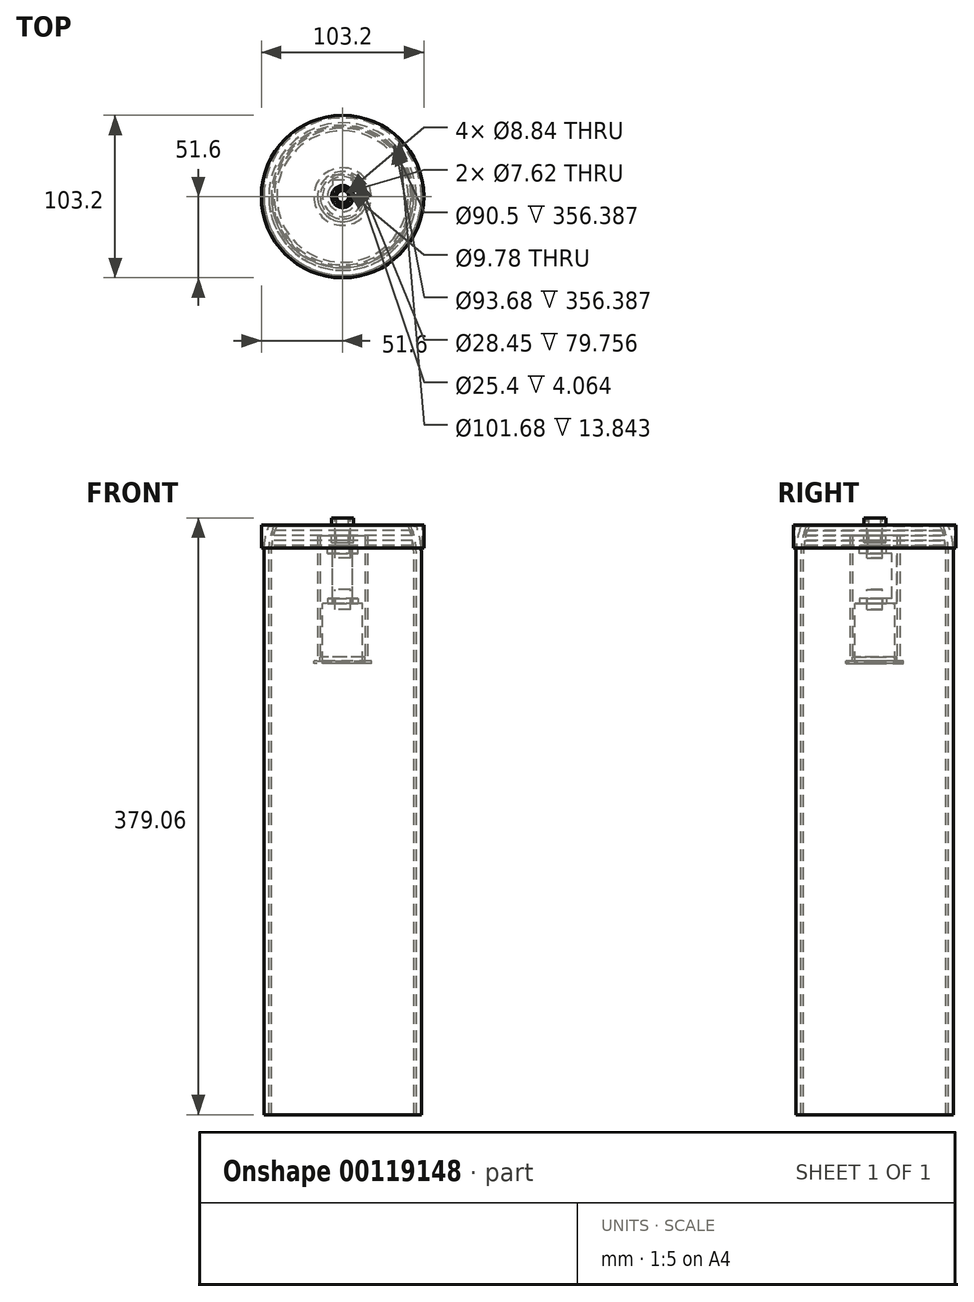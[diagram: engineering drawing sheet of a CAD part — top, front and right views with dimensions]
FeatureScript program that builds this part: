
annotation { "Feature Type Name" : "Feature", "Feature Type Description" : "" }
export const myFeature = defineFeature(function(context is Context, id is Id, definition is map)
    precondition{}
    {
        {
            var Q0;
            Q0=qCreatedBy(makeId("Front.planeOp"),FACE);
            var sketch = newSketch(context, id + "F0", { "sketchPlane" : qUnion([Q0])});
            skLineSegment(sketch, "E0", {"start": v(-50.01, -19.05) * mm, "end": v(-50.01, -375.44) * mm});
            skArc(sketch, "E1", {"start": v(-50.01, -19.05) * mm, "mid": v(-35.36, 16.31) * mm, "end": v(0, 30.96) * mm});
            skLineSegment(sketch, "E2", {"start": v(-50.01, -375.44) * mm, "end": v(0, -375.44) * mm});
            skLineSegment(sketch, "E3", {"start": v(0, 30.96) * mm, "end": v(0, -375.44) * mm});
            skSolve(sketch);
        }
        {
            var Q0;
            Q0=makeQuery(id+"F0.imprint","IMPRINT",FACE,{"disambiguationData":[TD([[makeQuery(id+"F0.imprint","IMPRINT",EDGE,{"derivedFrom":sQuery(id+"F0.wireOp",EDGE,"E0")}),1.0]])]});
            var Q1;
            Q1=sQuery(id+"F0.wireOp",EDGE,"E3");
            revolve(context, id + "F1", {"entities" : qUnion([Q0]), "axis" : qUnion([Q1]), "revolveType" : RevolveType.FULL});
        }
        {
            var Q0;
            Q0=qSketchRegion(id+"F0",true);
            var Q1;
            Q1=sQuery(id+"F0.wireOp",EDGE,"E3");
            revolve(context, id + "F2", {"entities" : qUnion([Q0]), "axis" : qUnion([Q1]), "revolveType" : RevolveType.FULL});
        }
        {
            var Q0;
            Q0=makeQuery(id+"F1.opRevolve","SWEPT_FACE",FACE,{"disambiguationData":[OSD([sQuery(id+"F0.wireOp",EDGE,"E2")])]});
            shell(context, id + "F3", {"entities" : qUnion([Q0]), "thickness" : 3.17 * mm});
        }
        {
            var Q0;
            Q0=makeQuery(id+"F2.opRevolve","SWEPT_FACE",FACE,{"disambiguationData":[OSD([sQuery(id+"F0.wireOp",EDGE,"E2")])]});
            shell(context, id + "F4", {"entities" : qUnion([Q0]), "thickness" : 4.76 * mm});
        }
        {
            var Q0;
            Q0=qCreatedBy(makeId("Front.planeOp"),FACE);
            var sketch = newSketch(context, id + "F5", { "sketchPlane" : qUnion([Q0])});
            skLineSegment(sketch, "E4", {"start": v(-97, -1.59) * mm, "end": v(106.2, -1.59) * mm});
            skArc(sketch, "E5", {"start": v(-50.01, -19.05) * mm, "mid": v(0, 30.96) * mm, "end": v(50.01, -19.05) * mm, "construction": true});
            skArc(sketch, "E6", {"start": v(-50.01, -19.05) * mm, "mid": v(0, 30.96) * mm, "end": v(50.01, -19.05) * mm});
            skSolve(sketch);
        }
        {
            var Q0;
            Q0=qSketchRegion(id+"F5",true);
            extrude(context, id + "F6", {"entities" : qUnion([Q0]), "operationType" : NewBodyOperationType.REMOVE, "endBound" : BoundingType.THROUGH_ALL, "oppositeDirection" : true, "depth" : 25.4 * mm, "hasSecondDirection" : true, "secondDirectionBound" : BoundingType.THROUGH_ALL, "secondDirectionOppositeDirection" : false, "secondDirectionDepth" : 25.4 * mm});
        }
        {
            var Q0;
            Q0=qCreatedBy(makeId("Front.planeOp"),FACE);
            var sketch = newSketch(context, id + "F7", { "sketchPlane" : qUnion([Q0])});
            skArc(sketch, "E7", {"start": v(43.46, -1.59) * mm, "mid": v(45.99, -10.16) * mm, "end": v(46.84, -19.05) * mm, "construction": true});
            skArc(sketch, "E8", {"start": v(-46.84, -19.05) * mm, "mid": v(-45.99, -10.16) * mm, "end": v(-43.46, -1.59) * mm, "construction": true});
            skLineSegment(sketch, "E9", {"start": v(-46.84, -19.05) * mm, "end": v(-46.84, -375.44) * mm, "construction": true});
            skLineSegment(sketch, "E10", {"start": v(46.84, -375.44) * mm, "end": v(46.84, -19.05) * mm, "construction": true});
            skLineSegment(sketch, "E11", {"start": v(43.46, -1.59) * mm, "end": v(46.86, -1.59) * mm, "construction": true});
            skLineSegment(sketch, "E12", {"start": v(-46.86, -1.59) * mm, "end": v(-43.46, -1.59) * mm, "construction": true});
            skArc(sketch, "E13", {"start": v(46.86, -1.59) * mm, "mid": v(49.22, -10.18) * mm, "end": v(50.01, -19.05) * mm, "construction": true});
            skArc(sketch, "E14", {"start": v(-50.01, -19.05) * mm, "mid": v(-49.22, -10.18) * mm, "end": v(-46.86, -1.59) * mm, "construction": true});
            skLineSegment(sketch, "E15", {"start": v(-50.01, -19.05) * mm, "end": v(-50.01, -375.44) * mm, "construction": true});
            skLineSegment(sketch, "E16", {"start": v(50.01, -375.44) * mm, "end": v(50.01, -19.05) * mm, "construction": true});
            skLineSegment(sketch, "E17", {"start": v(46.84, -375.44) * mm, "end": v(50.01, -375.44) * mm, "construction": true});
            skLineSegment(sketch, "E18", {"start": v(-50.01, -375.44) * mm, "end": v(-46.84, -375.44) * mm, "construction": true});
            skLineSegment(sketch, "E19", {"start": v(-51.6, -15.43) * mm, "end": v(-51.6, -0.83) * mm});
            skLineSegment(sketch, "E20", {"start": v(-51.6, -0.83) * mm, "end": v(-4.42, -0.83) * mm});
            skLineSegment(sketch, "E21", {"start": v(-4.42, -0.83) * mm, "end": v(-4.42, -1.59) * mm});
            skLineSegment(sketch, "E22", {"start": v(-44.45, -7.46) * mm, "end": v(-4.42, -7.46) * mm});
            skLineSegment(sketch, "E23", {"start": v(-4.42, -7.46) * mm, "end": v(-4.42, -4.29) * mm});
            skLineSegment(sketch, "E24", {"start": v(-51.6, -15.43) * mm, "end": v(-50.84, -15.43) * mm});
            skLineSegment(sketch, "E25", {"start": v(-44.45, -4.29) * mm, "end": v(-4.42, -4.29) * mm});
            skLineSegment(sketch, "E26", {"start": v(-50.84, -1.59) * mm, "end": v(-50.84, -15.43) * mm});
            skLineSegment(sketch, "E27", {"start": v(0, 0) * mm, "end": v(0, -375.44) * mm, "construction": true});
            skLineSegment(sketch, "E28", {"start": v(-50.84, -1.59) * mm, "end": v(-4.42, -1.59) * mm});
            skLineSegment(sketch, "E29", {"start": v(-44.45, -4.29) * mm, "end": v(-44.45, -7.46) * mm});
            skLineSegment(sketch, "E30", {"start": v(-43.73, -2.29) * mm, "end": v(43.73, -2.29) * mm, "construction": true});
            skSolve(sketch);
        }
        {
            var Q0;
            {var subQ1=sQuery(id+"F7.wireOp",EDGE,"E19");Q0=makeQuery(id+"F7.imprint","IMPRINT",FACE,{"disambiguationData":[TD([[makeQuery(id+"F7.imprint","IMPRINT",EDGE,{"derivedFrom":subQ1}),-1.0]])]});}
            var Q1;
            Q1=sQuery(id+"F7.wireOp",EDGE,"E27");
            revolve(context, id + "F8", {"entities" : qUnion([Q0]), "axis" : qUnion([Q1]), "revolveType" : RevolveType.FULL});
        }
        {
            var Q0;
            Q0=makeQuery(id+"F7.imprint","IMPRINT",FACE,{"disambiguationData":[TD([[makeQuery(id+"F7.imprint","IMPRINT",EDGE,{"derivedFrom":sQuery(id+"F7.wireOp",EDGE,"E22")}),1.0]])]});
            var Q1;
            Q1=sQuery(id+"F7.wireOp",EDGE,"E27");
            revolve(context, id + "F9", {"entities" : qUnion([Q0]), "axis" : qUnion([Q1]), "revolveType" : RevolveType.FULL});
        }
        {
            var Q0;
            Q0=makeQuery(id+"F8.opRevolve","SWEPT_FACE",FACE,{"disambiguationData":[OSD([sQuery(id+"F7.wireOp",EDGE,"E20")])]});
            cPlane(context, id + "F10", {"entities" : qUnion([Q0]), "cplaneType" : CPlaneType.OFFSET, "offset" : 4.44 * mm, "width" : 152.4 * mm, "height" : 152.4 * mm});
        }
        {
            var Q0;
            Q0=qCreatedBy(id+"F10.planeOp",FACE);
            var sketch = newSketch(context, id + "F11", { "sketchPlane" : qUnion([Q0])});
            skCircle(sketch, "E31", {"center": v(0, 0) * mm, "radius": 6.99 * mm});
            skCircle(sketch, "E32", {"center": v(0, 0) * mm, "radius": 3.81 * mm});
            skSolve(sketch);
        }
        {
            var Q0;
            Q0=makeQuery(id+"F11.imprint","IMPRINT",FACE,{"disambiguationData":[TD([[makeQuery(id+"F11.imprint","IMPRINT",EDGE,{"derivedFrom":sQuery(id+"F11.wireOp",EDGE,"E31")}),1.0]])]});
            extrude(context, id + "F12", {"entities" : qUnion([Q0]), "oppositeDirection" : true, "depth" : 4.44 * mm});
        }
        {
            var Q0;
            Q0=makeQuery(id+"F12.opExtrude","CAP_FACE",FACE,{"disambiguationData":[OSD([sQuery(id+"F11.wireOp",EDGE,"E31"),sQuery(id+"F11.wireOp",EDGE,"E32")])],"isStart":true});
            var sketch = newSketch(context, id + "F13", { "sketchPlane" : qUnion([Q0])});
            skCircle(sketch, "E33", {"center": v(0, 0) * mm, "radius": 4.93 * mm});
            skSolve(sketch);
        }
        {
            var Q0;
            Q0 = qSketchRegion(id + "F13", true);
            extrude(context, id + "F14", {"entities" : qUnion([Q0]), "oppositeDirection" : true, "depth" : 25.4 * mm});
        }
        {
            var Q0;
            Q0=makeQuery(id+"F9.opRevolve","SWEPT_FACE",FACE,{"disambiguationData":[OSD([sQuery(id+"F7.wireOp",EDGE,"E22")])]});
            var sketch = newSketch(context, id + "F15", { "sketchPlane" : qUnion([Q0])});
            skCircle(sketch, "E34", {"center": v(0, 0) * mm, "radius": 3.81 * mm});
            skCircle(sketch, "E35.0", {"center": v(0, 0) * mm, "radius": 6.99 * mm});
            skSolve(sketch);
        }
        {
            var Q0;
            Q0 = qSketchRegion(id + "F15", true);
            extrude(context, id + "F16", {"entities" : qUnion([Q0]), "depth" : 4.44 * mm});
        }
        {
            var Q0;
            Q0=makeQuery(id+"F16.opExtrude","CAP_FACE",FACE,{"disambiguationData":[OSD([sQuery(id+"F15.wireOp",EDGE,"E34"),sQuery(id+"F15.wireOp",EDGE,"E35.0")])],"isStart":false});
            cPlane(context, id + "F17", {"entities" : qUnion([Q0]), "cplaneType" : CPlaneType.OFFSET, "offset" : 3.8 * mm, "width" : 152.4 * mm, "height" : 152.4 * mm});
        }
        {
            var Q0;
            Q0=qCreatedBy(id+"F17.planeOp",FACE);
            var sketch = newSketch(context, id + "F18", { "sketchPlane" : qUnion([Q0])});
            skArc(sketch, "E36", {"start": v(6.35, -7.27) * mm, "mid": v(0, 9.65) * mm, "end": v(-6.35, -7.27) * mm});
            skCircle(sketch, "E37", {"center": v(0, 0) * mm, "radius": 4.42 * mm});
            skLineSegment(sketch, "E38.bottom", {"start": v(-6.35, -13.97) * mm, "end": v(6.35, -13.97) * mm});
            skLineSegment(sketch, "E38.left", {"start": v(-6.35, -13.97) * mm, "end": v(-6.35, -7.27) * mm});
            skLineSegment(sketch, "E38.right", {"start": v(6.35, -13.97) * mm, "end": v(6.35, -7.27) * mm});
            skSolve(sketch);
        }
        {
            var Q0;
            Q0=qSketchRegion(id+"F18",true);
            extrude(context, id + "F19", {"entities" : qUnion([Q0]), "depth" : 3.17 * mm});
        }
        {
            var Q0;
            Q0=makeQuery(id+"F19.opExtrude","CAP_FACE",FACE,{"disambiguationData":[OSD([sQuery(id+"F18.wireOp",EDGE,"E36"),sQuery(id+"F18.wireOp",EDGE,"E37"),sQuery(id+"F18.wireOp",EDGE,"E38.bottom"),sQuery(id+"F18.wireOp",EDGE,"E38.left"),sQuery(id+"F18.wireOp",EDGE,"E38.right")])],"isStart":false});
            var sketch = newSketch(context, id + "F20", { "sketchPlane" : qUnion([Q0])});
            skLineSegment(sketch, "E39.bottom", {"start": v(-6.35, -13.97) * mm, "end": v(6.35, -13.97) * mm});
            skLineSegment(sketch, "E39.top", {"start": v(-6.35, -10.8) * mm, "end": v(6.35, -10.8) * mm});
            skLineSegment(sketch, "E39.left", {"start": v(-6.35, -13.97) * mm, "end": v(-6.35, -10.8) * mm});
            skLineSegment(sketch, "E39.right", {"start": v(6.35, -13.97) * mm, "end": v(6.35, -10.8) * mm});
            skSolve(sketch);
        }
        {
            var Q0;
            Q0=qSketchRegion(id+"F20",true);
            extrude(context, id + "F21", {"entities" : qUnion([Q0]), "operationType" : NewBodyOperationType.ADD, "depth" : 31.75 * mm - 1 / 203.2 * mm});
        }
        {
            var Q0;
            Q0=makeQuery(id+"F21.opExtrude","CAP_FACE",FACE,{"disambiguationData":[OSD([sQuery(id+"F20.wireOp",EDGE,"E39.bottom"),sQuery(id+"F20.wireOp",EDGE,"E39.top"),sQuery(id+"F20.wireOp",EDGE,"E39.left"),sQuery(id+"F20.wireOp",EDGE,"E39.right")])],"isStart":false});
            var sketch = newSketch(context, id + "F22", { "sketchPlane" : qUnion([Q0])});
            skLineSegment(sketch, "E40.0.0", {"start": v(-6.35, -7.27) * mm, "end": v(-6.35, -10.8) * mm});
            skLineSegment(sketch, "E40.0.1", {"start": v(-6.35, -10.8) * mm, "end": v(6.35, -10.8) * mm});
            skLineSegment(sketch, "E40.0.2", {"start": v(6.35, -10.8) * mm, "end": v(6.35, -7.27) * mm});
            skArc(sketch, "E40.0.3", {"start": v(6.35, -7.27) * mm, "mid": v(0, 9.65) * mm, "end": v(-6.35, -7.27) * mm});
            skLineSegment(sketch, "E41.0", {"start": v(-6.35, -13.97) * mm, "end": v(6.35, -13.97) * mm});
            skLineSegment(sketch, "E41.2", {"start": v(-6.35, -13.97) * mm, "end": v(-6.35, -10.8) * mm});
            skLineSegment(sketch, "E41.3", {"start": v(6.35, -13.97) * mm, "end": v(6.35, -10.8) * mm});
            skCircle(sketch, "E42.0", {"center": v(0, 0) * mm, "radius": 4.89 * mm});
            skSolve(sketch);
        }
        {
            var Q0;
            Q0=qSketchRegion(id+"F22",true);
            extrude(context, id + "F23", {"entities" : qUnion([Q0]), "operationType" : NewBodyOperationType.ADD, "oppositeDirection" : true, "depth" : 3.17 * mm});
        }
        {
            var Q0;
            Q0=qCreatedBy(makeId("Front.planeOp"),FACE);
            var sketch = newSketch(context, id + "F24", { "sketchPlane" : qUnion([Q0])});
            skLineSegment(sketch, "E43.bottom", {"start": v(-4.93, -41.75) * mm, "end": v(4.93, -41.75) * mm});
            skLineSegment(sketch, "E43.top", {"start": v(-4.93, -54.45) * mm, "end": v(4.93, -54.45) * mm});
            skLineSegment(sketch, "E43.left", {"start": v(-4.93, -41.75) * mm, "end": v(-4.93, -54.45) * mm});
            skLineSegment(sketch, "E43.right", {"start": v(4.93, -41.75) * mm, "end": v(4.93, -54.45) * mm});
            skLineSegment(sketch, "E44", {"start": v(-4.93, 3.62) * mm, "end": v(-4.93, -21.78) * mm});
            skLineSegment(sketch, "E45", {"start": v(4.93, -21.78) * mm, "end": v(4.93, 3.62) * mm});
            skLineSegment(sketch, "E46.bottom", {"start": v(-12.7, -50.64) * mm, "end": v(12.7, -50.64) * mm});
            skLineSegment(sketch, "E46.top", {"start": v(-12.7, -88.74) * mm, "end": v(12.7, -88.74) * mm});
            skLineSegment(sketch, "E46.left", {"start": v(-12.7, -50.64) * mm, "end": v(-12.7, -88.74) * mm});
            skLineSegment(sketch, "E46.right", {"start": v(12.7, -50.64) * mm, "end": v(12.7, -88.74) * mm});
            skLineSegment(sketch, "E47", {"start": v(-12.7, -84.68) * mm, "end": v(-14.22, -84.68) * mm});
            skLineSegment(sketch, "E48", {"start": v(-14.22, -84.68) * mm, "end": v(-14.22, -87.22) * mm});
            skLineSegment(sketch, "E49", {"start": v(-14.22, -87.22) * mm, "end": v(-18.29, -87.22) * mm});
            skLineSegment(sketch, "E50", {"start": v(-18.29, -87.22) * mm, "end": v(-18.29, -88.74) * mm});
            skLineSegment(sketch, "E51", {"start": v(-18.29, -88.74) * mm, "end": v(-12.7, -88.74) * mm});
            skLineSegment(sketch, "E52", {"start": v(0, -41.75) * mm, "end": v(0, -88.74) * mm});
            skSolve(sketch);
        }
        {
            var Q0;
            Q0=makeQuery(id+"F9.opRevolve","SWEPT_BODY",BODY,{"disambiguationData":[OSD([sQuery(id+"F7.wireOp",EDGE,"E22"),sQuery(id+"F7.wireOp",EDGE,"Ugg7gFXu-7LBC-ZnE3-bfDh-bOkt1AxjQZup"),sQuery(id+"F7.wireOp",EDGE,"raBS2b0A-6G7s-Fj2a-Zl0Q-qt7Aqct4Q4Jh"),sQuery(id+"F7.wireOp",EDGE,"E23"),sQuery(id+"F7.wireOp",EDGE,"E25"),sQuery(id+"F7.wireOp",EDGE,"GcN3Lvol-L1Fh-g2yS-zhSm-u6JfP0j2qKPq.bottom"),sQuery(id+"F7.wireOp",EDGE,"E29")])]});
            var Q1;
            Q1=sQuery(id+"F0.wireOp",EDGE,"E3");
            var Q2;
            Q2=sQuery(id+"F0.wireOp",EDGE,"E3");
            transform(context, id + "F25", {"entities" : qUnion([Q0]), "transformType" : TransformType.TRANSLATION_DISTANCE, "transformDirection" : qUnion([Q2]), "distance" : 6.4 * mm, "makeCopy" : true});
        }
        {
            var Q0;
            {var subQ0=sQuery(id+"F24.wireOp",EDGE,"E43.left");var subQ1=sQuery(id+"F24.wireOp",EDGE,"E43.bottom");var subQ2=makeQuery(id+"F24.imprint","INTERSECT",VERTEX,{"derivedFrom":[subQ1,subQ0]});Q0=makeQuery(id+"F24.imprint","IMPRINT",FACE,{"disambiguationData":[TD([[makeQuery(id+"F24.imprint","IMPRINT",EDGE,{"disambiguationData":[TD([[subQ2,-1.0]])],"derivedFrom":subQ1}),-1.0]])]});}
            var Q1;
            {var subQ0=sQuery(id+"F24.wireOp",EDGE,"E43.left");var subQ1=sQuery(id+"F24.wireOp",EDGE,"E43.top");var subQ2=makeQuery(id+"F24.imprint","INTERSECT",VERTEX,{"derivedFrom":[subQ1,subQ0]});Q1=makeQuery(id+"F24.imprint","IMPRINT",FACE,{"disambiguationData":[TD([[makeQuery(id+"F24.imprint","IMPRINT",EDGE,{"disambiguationData":[TD([[subQ2,-1.0]])],"derivedFrom":subQ1}),1.0]])]});}
            var Q2;
            Q2=sQuery(id+"F24.wireOp",EDGE,"E52");
            revolve(context, id + "F26", {"entities" : qUnion([Q0, Q1]), "axis" : qUnion([Q2]), "revolveType" : RevolveType.FULL});
        }
        {
            var Q0;
            {var subQ0=sQuery(id+"F24.wireOp",EDGE,"E43.left");var subQ1=sQuery(id+"F24.wireOp",EDGE,"E43.top");var subQ2=makeQuery(id+"F24.imprint","INTERSECT",VERTEX,{"derivedFrom":[subQ1,subQ0]});Q0=makeQuery(id+"F24.imprint","IMPRINT",FACE,{"disambiguationData":[TD([[makeQuery(id+"F24.imprint","IMPRINT",EDGE,{"disambiguationData":[TD([[subQ2,-1.0]])],"derivedFrom":subQ1}),1.0]])]});}
            var Q1;
            {var subQ5=sQuery(id+"F24.wireOp",EDGE,"E43.top");var subQ9=sQuery(id+"F24.wireOp",EDGE,"E43.left");var subQ11=makeQuery(id+"F24.imprint","INTERSECT",VERTEX,{"derivedFrom":[subQ5,subQ9]});Q1=makeQuery(id+"F24.imprint","IMPRINT",FACE,{"disambiguationData":[TD([[makeQuery(id+"F24.imprint","IMPRINT",EDGE,{"disambiguationData":[TD([[subQ11,-1.0]])],"derivedFrom":subQ5}),-1.0]])]});}
            var Q2;
            Q2=sQuery(id+"F24.wireOp",EDGE,"E52");
            revolve(context, id + "F27", {"entities" : qUnion([Q0, Q1]), "axis" : qUnion([Q2]), "revolveType" : RevolveType.FULL});
        }
        {
            var Q0;
            {var subQ0=sQuery(id+"F24.wireOp",EDGE,"E47");Q0=makeQuery(id+"F24.imprint","IMPRINT",FACE,{"disambiguationData":[TD([[makeQuery(id+"F24.imprint","IMPRINT",EDGE,{"derivedFrom":subQ0}),1.0]])]});}
            var Q1;
            Q1=sQuery(id+"F24.wireOp",EDGE,"E52");
            revolve(context, id + "F28", {"entities" : qUnion([Q0]), "axis" : qUnion([Q1]), "revolveType" : RevolveType.FULL});
        }
        {
            var Q0;
            Q0=makeQuery(id+"F28.opRevolve","SWEPT_FACE",FACE,{"disambiguationData":[OSD([sQuery(id+"F24.wireOp",EDGE,"E49")])]});
            var sketch = newSketch(context, id + "F29", { "sketchPlane" : qUnion([Q0])});
            skCircle(sketch, "E53", {"center": v(0, 0) * mm, "radius": 15.88 * mm});
            skCircle(sketch, "E54", {"center": v(0, 0) * mm, "radius": 14.2 * mm});
            skSolve(sketch);
        }
        {
            var Q0;
            Q0=makeQuery(id+"F29.imprint","IMPRINT",FACE,{"disambiguationData":[TD([[makeQuery(id+"F29.imprint","IMPRINT",EDGE,{"derivedFrom":sQuery(id+"F29.wireOp",EDGE,"E53")}),1.0]])]});
            var Q1;
            Q1=makeQuery(id+"F9.opRevolve","SWEPT_FACE",FACE,{"disambiguationData":[OSD([sQuery(id+"F7.wireOp",EDGE,"E22")])]});
            extrude(context, id + "F30", {"entities" : qUnion([Q0]), "endBound" : BoundingType.UP_TO_SURFACE, "endBoundEntityFace" : qUnion([Q1]), "depth" : 76.2 * mm});
        }
    });
